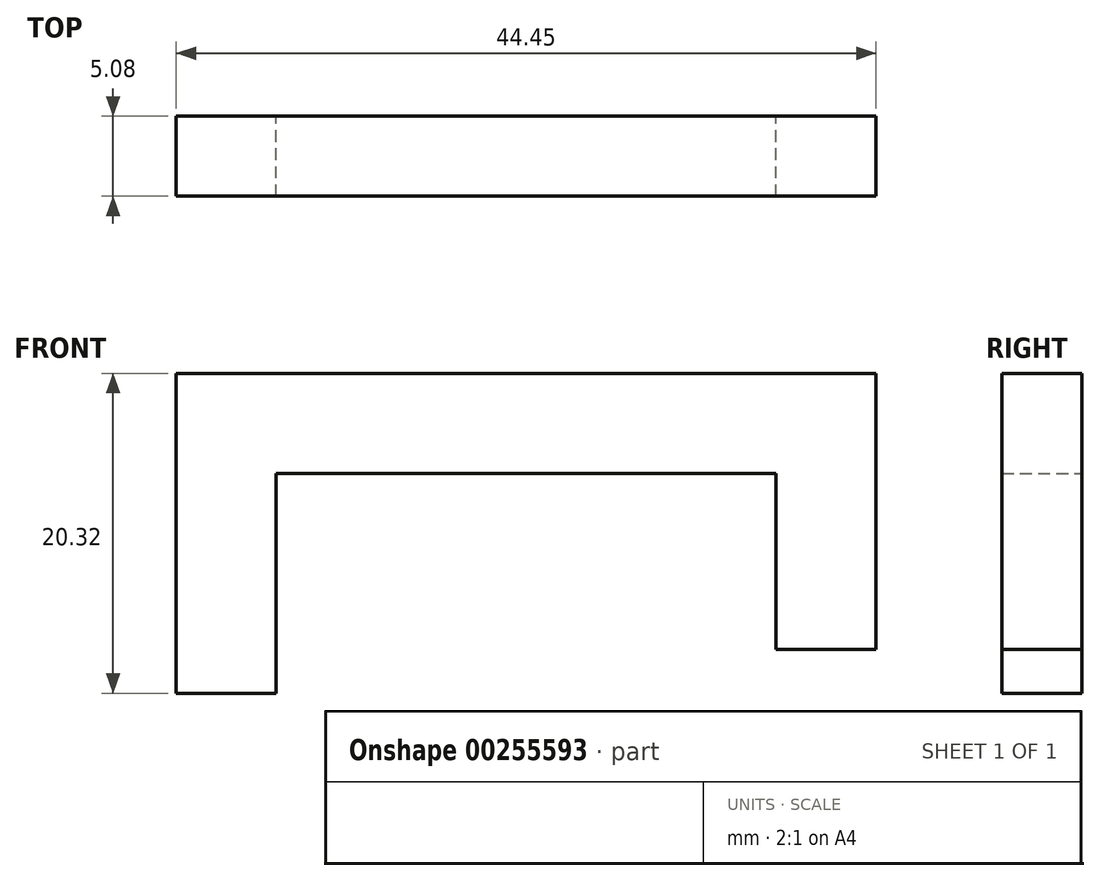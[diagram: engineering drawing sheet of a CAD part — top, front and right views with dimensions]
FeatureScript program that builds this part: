
annotation { "Feature Type Name" : "Feature", "Feature Type Description" : "" }
export const myFeature = defineFeature(function(context is Context, id is Id, definition is map)
    precondition{}
    {
        {
            var Q0;
            Q0=qCreatedBy(makeId("Front.planeOp"),FACE);
            var sketch = newSketch(context, id + "F0", { "sketchPlane" : qUnion([Q0])});
            skLineSegment(sketch, "E0.bottom", {"start": v(0, 0) * mm, "end": v(6.35, 0) * mm});
            skLineSegment(sketch, "E0.top", {"start": v(0, 20.32) * mm, "end": v(6.35, 20.32) * mm});
            skLineSegment(sketch, "E0.left", {"start": v(0, 0) * mm, "end": v(0, 20.32) * mm});
            skLineSegment(sketch, "E0.right", {"start": v(6.35, 0) * mm, "end": v(6.35, 13.97) * mm});
            skLineSegment(sketch, "E1.bottom", {"start": v(6.35, 20.32) * mm, "end": v(44.45, 20.32) * mm});
            skLineSegment(sketch, "E1.top", {"start": v(6.35, 13.97) * mm, "end": v(38.1, 13.97) * mm});
            skLineSegment(sketch, "E1.right", {"start": v(44.45, 20.32) * mm, "end": v(44.45, 13.97) * mm});
            skLineSegment(sketch, "E2.top", {"start": v(44.45, 2.78) * mm, "end": v(38.1, 2.78) * mm});
            skLineSegment(sketch, "E2.left", {"start": v(44.45, 13.97) * mm, "end": v(44.45, 2.78) * mm});
            skLineSegment(sketch, "E2.right", {"start": v(38.1, 13.97) * mm, "end": v(38.1, 2.78) * mm});
            skSolve(sketch);
        }
        {
            var Q0;
            Q0=makeQuery(id+"F0.imprint","IMPRINT",FACE,{"disambiguationData":[TD([[makeQuery(id+"F0.imprint","IMPRINT",EDGE,{"derivedFrom":sQuery(id+"F0.wireOp",EDGE,"E0.bottom")}),1.0]])]});
            extrude(context, id + "F1", {"entities" : qUnion([Q0]), "depth" : 5.08 * mm});
        }
    });
